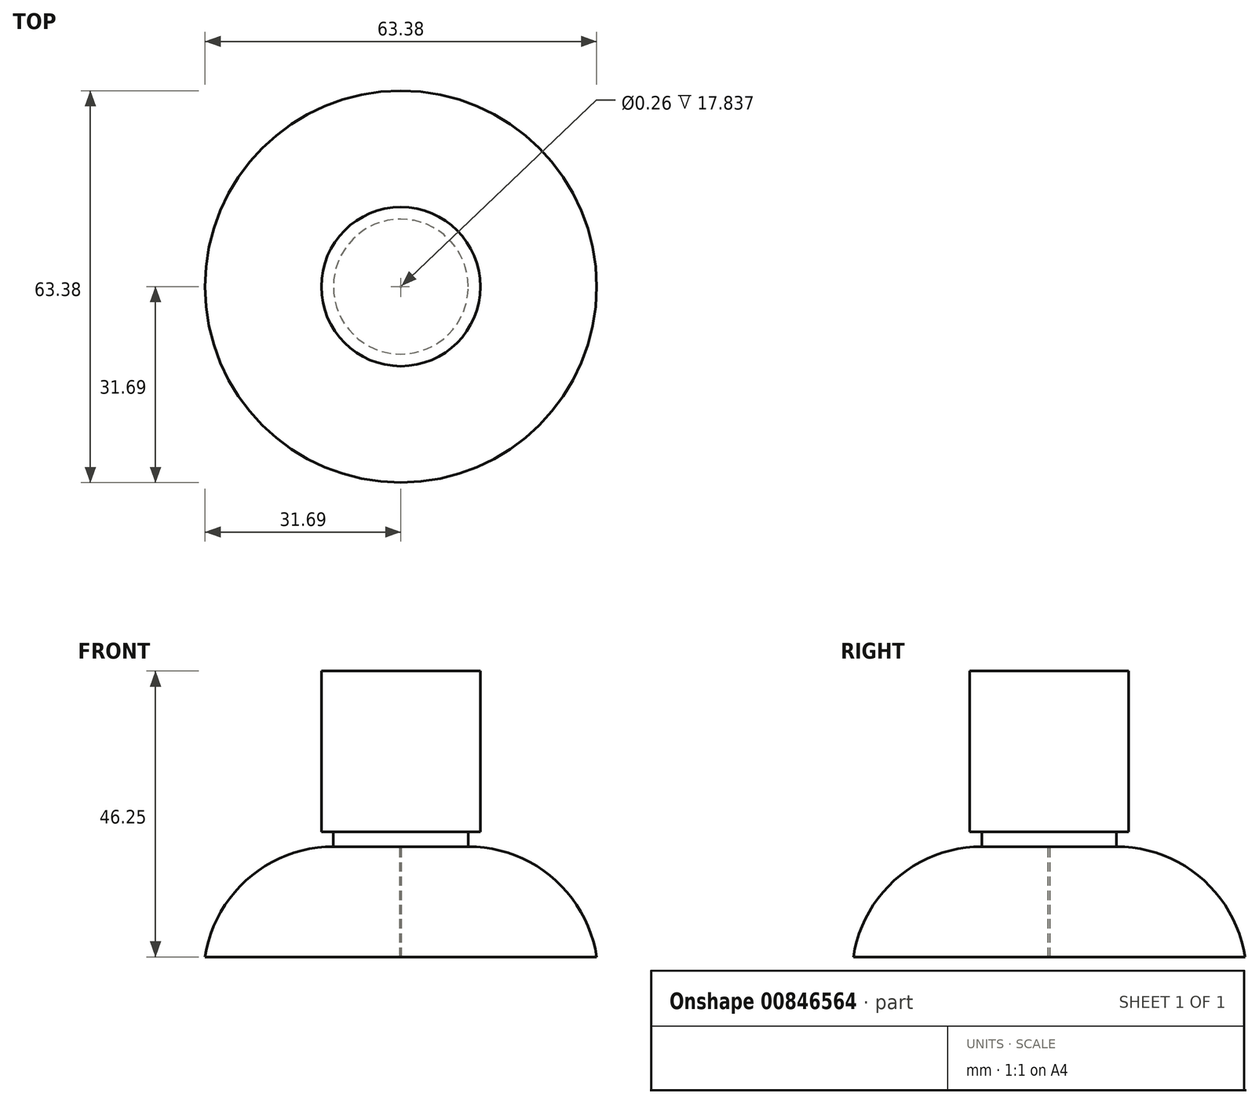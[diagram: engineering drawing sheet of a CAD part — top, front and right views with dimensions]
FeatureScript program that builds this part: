
annotation { "Feature Type Name" : "Feature", "Feature Type Description" : "" }
export const myFeature = defineFeature(function(context is Context, id is Id, definition is map)
    precondition{}
    {
        {
            var Q0;
            Q0=qCreatedBy(makeId("Front.planeOp"),FACE);
            var sketch = newSketch(context, id + "F0", { "sketchPlane" : qUnion([Q0])});
            skLineSegment(sketch, "E0.bottom", {"start": v(0, 26.03) * mm, "end": v(-12.87, 26.03) * mm});
            skLineSegment(sketch, "E0.top", {"start": v(0, 0) * mm, "end": v(-12.87, 0) * mm});
            skLineSegment(sketch, "E0.left", {"start": v(0, 26.03) * mm, "end": v(0, 0) * mm});
            skLineSegment(sketch, "E0.right", {"start": v(-12.87, 26.03) * mm, "end": v(-12.87, 0) * mm});
            skLineSegment(sketch, "E1.bottom", {"start": v(-10.92, 0) * mm, "end": v(0, 0) * mm});
            skLineSegment(sketch, "E1.top", {"start": v(-10.92, -2.38) * mm, "end": v(0, -2.38) * mm});
            skLineSegment(sketch, "E1.left", {"start": v(-10.92, 0) * mm, "end": v(-10.92, -2.38) * mm});
            skLineSegment(sketch, "E1.right", {"start": v(0, 0) * mm, "end": v(0, -2.38) * mm});
            skLineSegment(sketch, "E2.bottom", {"start": v(-10.92, -2.38) * mm, "end": v(-0.13, -2.38) * mm});
            skLineSegment(sketch, "E2.top", {"start": v(-10.92, -38.05) * mm, "end": v(-0.13, -38.05) * mm});
            skLineSegment(sketch, "E2.left", {"start": v(-10.92, -2.38) * mm, "end": v(-10.92, -38.05) * mm});
            skLineSegment(sketch, "E2.right", {"start": v(-0.13, -2.38) * mm, "end": v(-0.13, -38.05) * mm});
            skPoint(sketch, "E3.endSnap0", {"position": v(-10.92, -20.22) * mm});
            skLineSegment(sketch, "E4", {"start": v(-10.92, -20.22) * mm, "end": v(-0.13, -20.22) * mm});
            skLineSegment(sketch, "E5", {"start": v(-10.92, -20.22) * mm, "end": v(-31.69, -20.22) * mm});
            skLineSegment(sketch, "E6", {"start": v(-31.69, -20.22) * mm, "end": v(-10.92, -2.38) * mm});
            skArc(sketch, "E7", {"start": v(-10.92, -2.38) * mm, "mid": v(-24.6, -7.45) * mm, "end": v(-31.69, -20.22) * mm});
            skSolve(sketch);
        }
        {
            var Q0;
            Q0=makeQuery(id+"F0.imprint","IMPRINT",FACE,{"disambiguationData":[TD([[makeQuery(id+"F0.imprint","IMPRINT",EDGE,{"derivedFrom":sQuery(id+"F0.wireOp",EDGE,"E6")}),1.0]])]});
            var Q1;
            {var subQ2=sQuery(id+"F0.wireOp",EDGE,"E5");Q1=makeQuery(id+"F0.imprint","IMPRINT",FACE,{"disambiguationData":[TD([[makeQuery(id+"F0.imprint","IMPRINT",EDGE,{"derivedFrom":subQ2}),-1.0]])]});}
            var Q2;
            {var subQ0=sQuery(id+"F0.wireOp",EDGE,"E1.left");Q2=makeQuery(id+"F0.imprint","IMPRINT",FACE,{"disambiguationData":[TD([[makeQuery(id+"F0.imprint","IMPRINT",EDGE,{"derivedFrom":subQ0}),1.0]])]});}
            var Q3;
            {var subQ5=sQuery(id+"F0.wireOp",EDGE,"E4");Q3=makeQuery(id+"F0.imprint","IMPRINT",FACE,{"disambiguationData":[TD([[makeQuery(id+"F0.imprint","IMPRINT",EDGE,{"derivedFrom":subQ5}),1.0]])]});}
            var Q4;
            Q4=makeQuery(id+"F0.imprint","IMPRINT",FACE,{"disambiguationData":[TD([[makeQuery(id+"F0.imprint","IMPRINT",EDGE,{"derivedFrom":sQuery(id+"F0.wireOp",EDGE,"E0.bottom")}),1.0]])]});
            var Q5;
            Q5=sQuery(id+"F0.wireOp",EDGE,"E0.left");
            revolve(context, id + "F1", {"surfaceOperationType" : NewSurfaceOperationType.NEW, "entities" : qUnion([Q0, Q1, Q2, Q3, Q4]), "axis" : qUnion([Q5]), "revolveType" : RevolveType.FULL});
        }
    });
